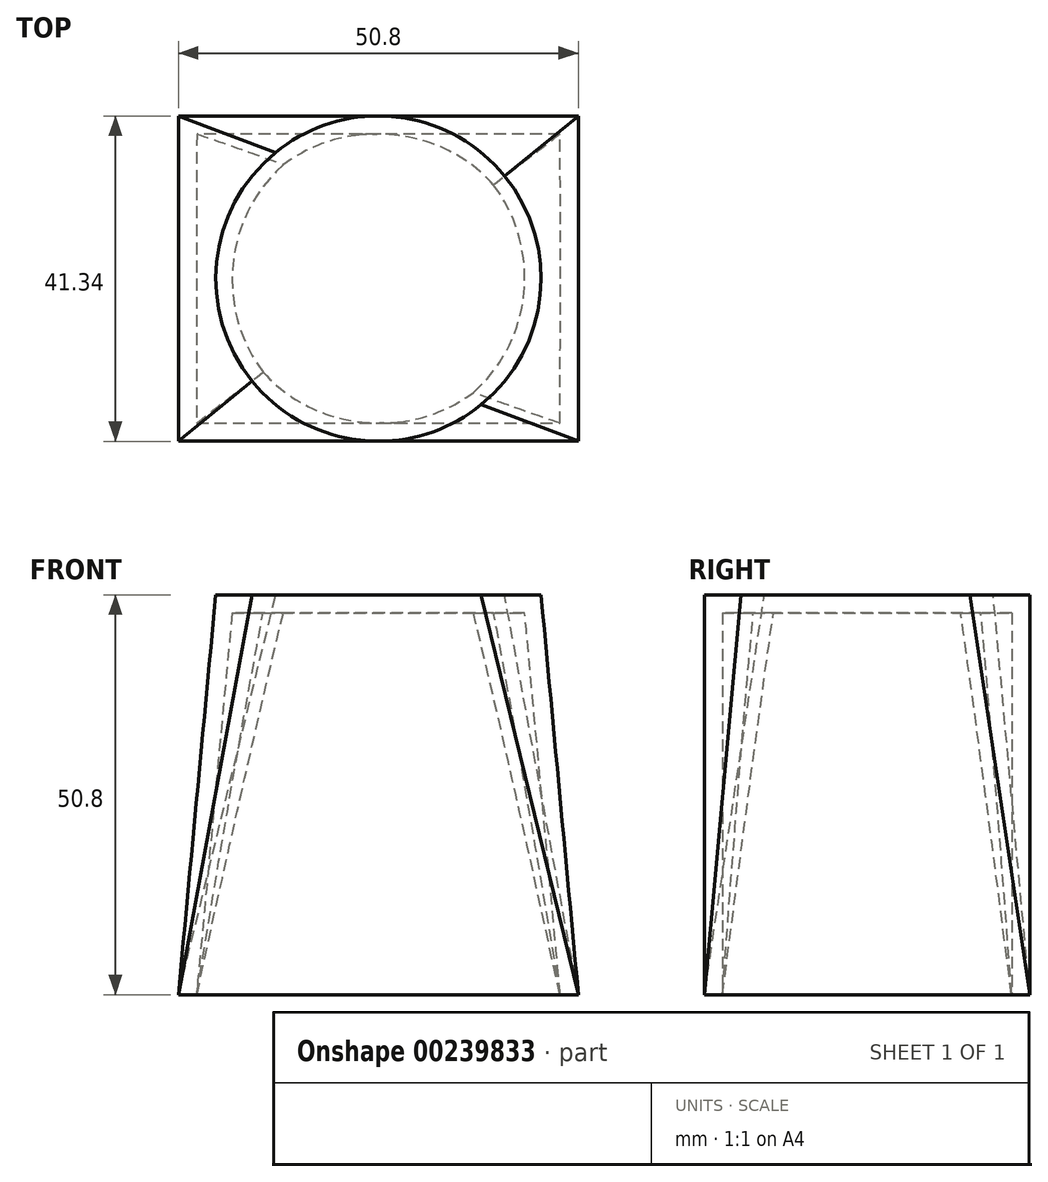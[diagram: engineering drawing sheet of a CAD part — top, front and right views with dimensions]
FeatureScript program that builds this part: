
annotation { "Feature Type Name" : "Feature", "Feature Type Description" : "" }
export const myFeature = defineFeature(function(context is Context, id is Id, definition is map)
    precondition{}
    {
        {
            var Q0;
            Q0=qCreatedBy(makeId("Top.planeOp"),FACE);
            var sketch = newSketch(context, id + "F0", { "sketchPlane" : qUnion([Q0])});
            skLineSegment(sketch, "E0.bottom", {"start": v(25.4, 20.67) * mm, "end": v(-25.4, 20.67) * mm});
            skLineSegment(sketch, "E0.top", {"start": v(25.4, -20.67) * mm, "end": v(-25.4, -20.67) * mm});
            skLineSegment(sketch, "E0.left", {"start": v(25.4, 20.67) * mm, "end": v(25.4, -20.67) * mm});
            skLineSegment(sketch, "E0.right", {"start": v(-25.4, 20.67) * mm, "end": v(-25.4, -20.67) * mm});
            skPoint(sketch, "E0.middle", {"position": v(0, 0) * mm});
            skSolve(sketch);
        }
        {
            var Q0;
            Q0=qCreatedBy(makeId("Top.planeOp"),FACE);
            cPlane(context, id + "F1", {"entities" : qUnion([Q0]), "cplaneType" : CPlaneType.OFFSET, "offset" : 50.8 * mm, "width" : 152.4 * mm, "height" : 152.4 * mm});
        }
        {
            var Q0;
            Q0=qCreatedBy(id+"F1.planeOp",FACE);
            var sketch = newSketch(context, id + "F2", { "sketchPlane" : qUnion([Q0])});
            skCircle(sketch, "E1", {"center": v(0, 0) * mm, "radius": 20.67 * mm});
            skSolve(sketch);
        }
        {
            var Q0;
            Q0=makeQuery(id+"F0.imprint","IMPRINT",FACE,{"disambiguationData":[TD([[makeQuery(id+"F0.imprint","IMPRINT",EDGE,{"derivedFrom":sQuery(id+"F0.wireOp",EDGE,"E0.bottom")}),1.0]])]});
            var Q1;
            Q1=makeQuery(id+"F2.imprint","IMPRINT",FACE,{"disambiguationData":[TD([[makeQuery(id+"F2.imprint","IMPRINT",EDGE,{"derivedFrom":sQuery(id+"F2.wireOp",EDGE,"E1")}),1.0]])]});
            loft(context, id + "F3", {"sheetProfilesArray" : [{ "sheetProfileEntities" : qUnion([Q0]) }, { "sheetProfileEntities" : qUnion([Q1]) }]});
        }
        {
            var Q0;
            Q0=makeQuery(id+"F3.opLoft","CAP_FACE",FACE,{"disambiguationData":[OSD([makeQuery(id+"F0.imprint","IMPRINT",FACE,{"disambiguationData":[TD([[makeQuery(id+"F0.imprint","IMPRINT",EDGE,{"derivedFrom":sQuery(id+"F0.wireOp",EDGE,"E0.bottom")}),1.0]])]})])],"isStart":true});
            shell(context, id + "F4", {"entities" : qUnion([Q0]), "thickness" : 2.3 * mm});
        }
    });
